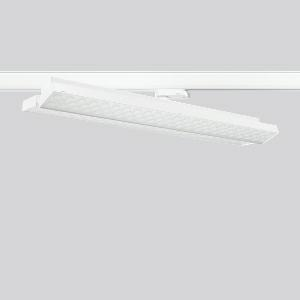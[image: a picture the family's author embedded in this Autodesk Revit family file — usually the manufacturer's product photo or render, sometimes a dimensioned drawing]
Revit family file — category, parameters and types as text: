
# Revit family: tx-move_742161_002_3_76_3072
name_source: partatom
category: Lighting Fixtures
units: mm (PartAtom-declared; Revit-internal decimal feet)

## family parameters
Cut with Voids When Loaded = No
Host = Face
Light Source = No
Part Type = Normal
Room Calculation Point = No
Round Connector Dimension = Use Diameter
Shared = No

## types (1)
- MultiLumen 1 (1 x LED Modul 835, 3025 lm, 3500)
    Apparent Load = 41 VA
    CIE Flux Codes = 88 96 99 100 100
    Color Rendering = 80
    Color Temperature = 3500
    Default Elevation = 1800 mm
    Description = Series: TX-MOVE
Multifunctional surface-mounted spotlight for area lighting. Very flat design. Housing: sheet steel, powder-coated. Rotation range: 356°. Swivel range: 90°. Consistent alignment possible with visible tilt scale. High-efficiency LED units with optimum light control thanks to clear plastic (PC) lens optics. Spezielle Mikrostrukturen reduzieren Gelbsaum. Symmetrical light distribution. With adapter for RZB 3-circuit DALI tracks. Suitable for Track on ceiling. MultiLumen: Luminous flux adjustable in 3 steps. Factory setting is the highest luminous flux. Environmentally friendly and resource-saving due to replaceable and recyclable components. 
Colour: traffic white, matt (RAL 9016)
Length: 570 mm
Width: 119 mm
Height: 88 mm
Lamp: LED
Socket: without socket
Colour temperature: 3500K
Colour rendering index (CRI): 80
System power: 41 W
Rated luminous flux: 6050 lm
Luminous efficiency: 148 lm/W
System power 2: 57 W
Rated luminous flux 2: 8200 lm
Luminous efficiency 2: 144 lm/W
System power 3: 73 W
Rated luminous flux 3: 10000 lm
Luminous efficiency 3: 137 lm/W
Control gear: Dimmable EVG, DALI
Protection class: I
Type of protection: IP 20
    Height = 75 mm
    Lamp = 1 x LED Modul 835
    Lamp Light Flux = 3025 lm
    Lamp count = 1
    Length = 569 mm
    Lifetime = 50000 h
    Luminous efficacy = 148 lm/W
    Manufacturer = RZB
    ModVariant = No
    Model = 742161.002.3.76
    Mounting Place = Ceiling
    Mounting Type = Rail mounted
    Number of Poles = 1
    OnlyDefault = Yes
    Power Factor = 1
    Product Name = TX-MOVE
    Product group = Track mounted projectors
    ProductGroupID = 301
    Protection Class = Protection class I
    Protection Degree = IP 20
    RLX_Detail_Level = 1
    RLX_Emergency_Light_Flux = 0 lm
    RLX_Emergency_Type = 0
    RLX_Emergency_Type_DB = No
    RlxData = <blob elided: 31217 chars, md5=3cc39f80>
    Socket = socket
    Standby Power = 0 W
    System Light Flux = 6050 lm
    System Power = 41 W
    Type Comments = MultiLumen 1
    Type Image = 742162.002.jpg
    URL = http://relux.com
    VarID = multilumen_1
    Voltage = 230 V
    Voltage Range = 220-240 V
    Weight = 0.00 kg
    Width = 119 mm

## geometry (parser evidence)
native form markers: Blend x4, Sweep x15
no freeform markers — native parametric forms only
